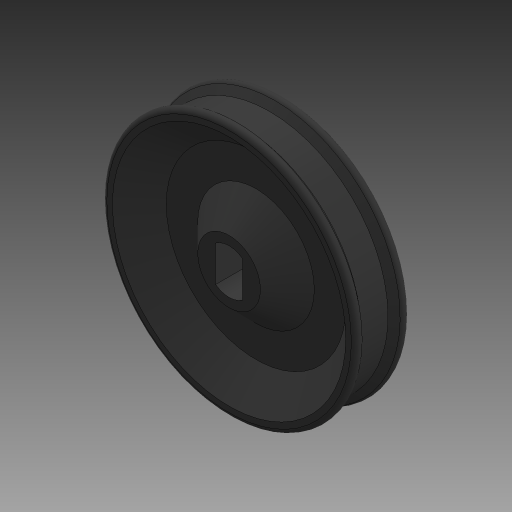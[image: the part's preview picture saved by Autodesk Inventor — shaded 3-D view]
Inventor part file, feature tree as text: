
AUTODESK INVENTOR PART (.ipt)
format: ipt  version: 2023 (Build 270158000, 158)  size: 364,032 bytes
history: native  units: mm
features: sketch x3, other x2, extrude x2, chamfer x2, fillet x1
ambient origin geometry x8: Origin, YZ Plane, XZ Plane, XY Plane, X Axis, Y Axis, Z Axis, Center Point
bodies: Body1 (feature_tree)
feature tree (10):
  other  "Těleso1"
  extrude  "Vysunutí1"  Depth=5.0mm
  other  "Rotace1"
  fillet  "Zaoblení1"  Radius=3.0mm
  extrude  "Vysunutí2"  Depth=5.0mm
  chamfer  "Zkosení1"  Distance=30.0mm
  chamfer  "Zkosení2"  Distance=6.0mm
  sketch  "Náčrt1"
  sketch  "Náčrt2"
  sketch  "Náčrt3"
